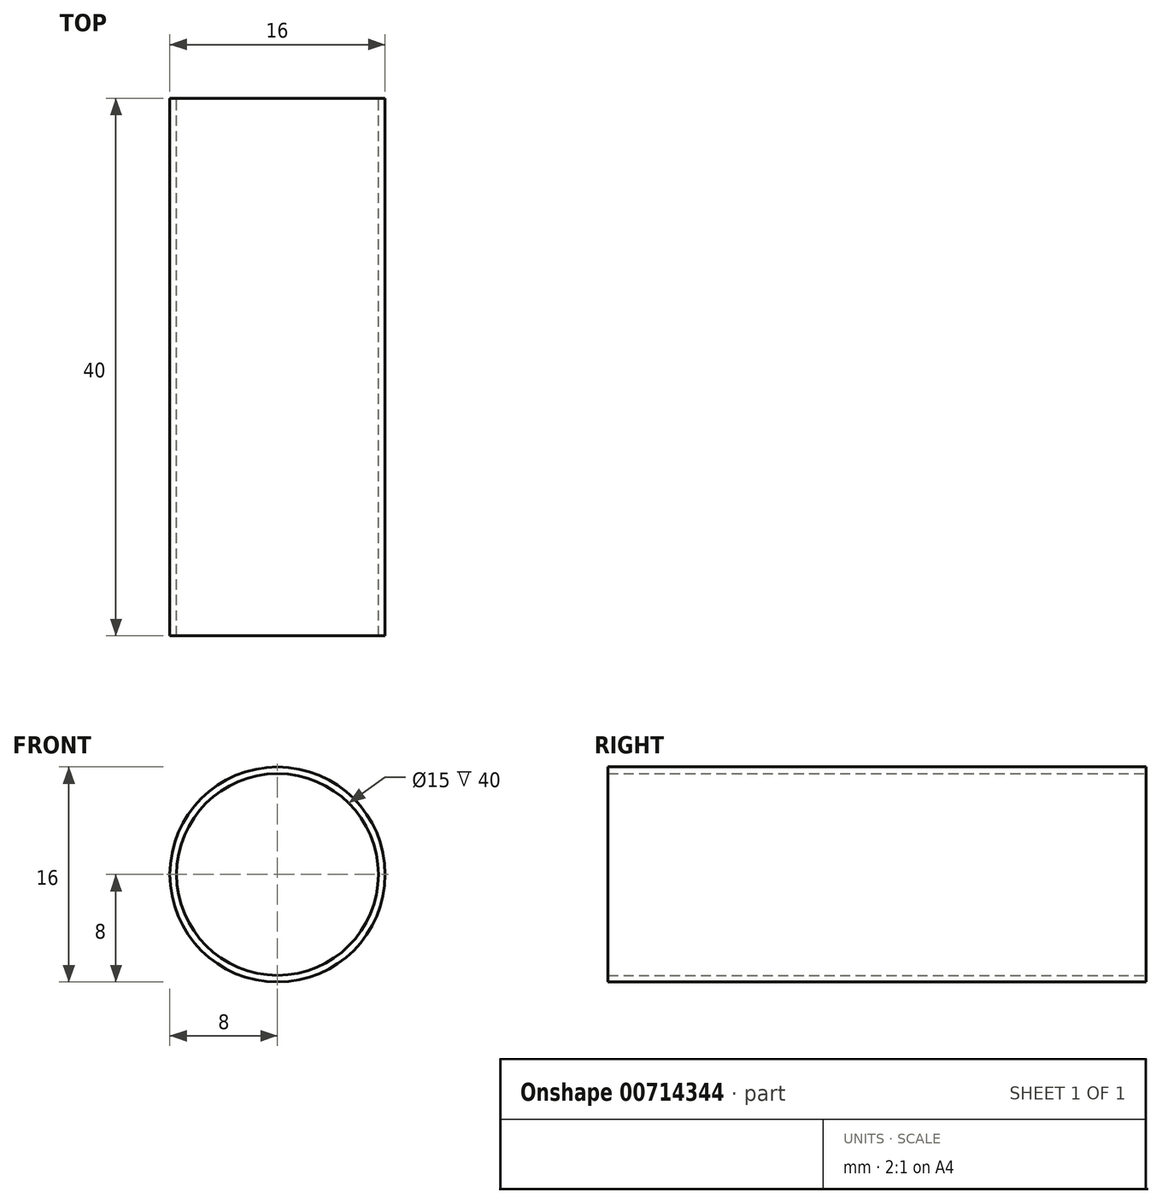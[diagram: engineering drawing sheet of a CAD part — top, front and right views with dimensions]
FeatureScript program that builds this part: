
annotation { "Feature Type Name" : "Feature", "Feature Type Description" : "" }
export const myFeature = defineFeature(function(context is Context, id is Id, definition is map)
    precondition{}
    {
        {
            var Q0;
            Q0=qCreatedBy(makeId("Front.planeOp"),FACE);
            var sketch = newSketch(context, id + "F0", { "sketchPlane" : qUnion([Q0])});
            skCircle(sketch, "E0", {"center": v(0, 0) * mm, "radius": 8 * mm});
            skCircle(sketch, "E1", {"center": v(0, 0) * mm, "radius": 7.5 * mm});
            skSolve(sketch);
        }
        {
            var Q0;
            Q0=qSketchRegion(id+"F0",true);
            extrude(context, id + "F1", {"entities" : qUnion([Q0]), "depth" : 40 * mm, "offsetDistance" : 25 * mm});
        }
    });
